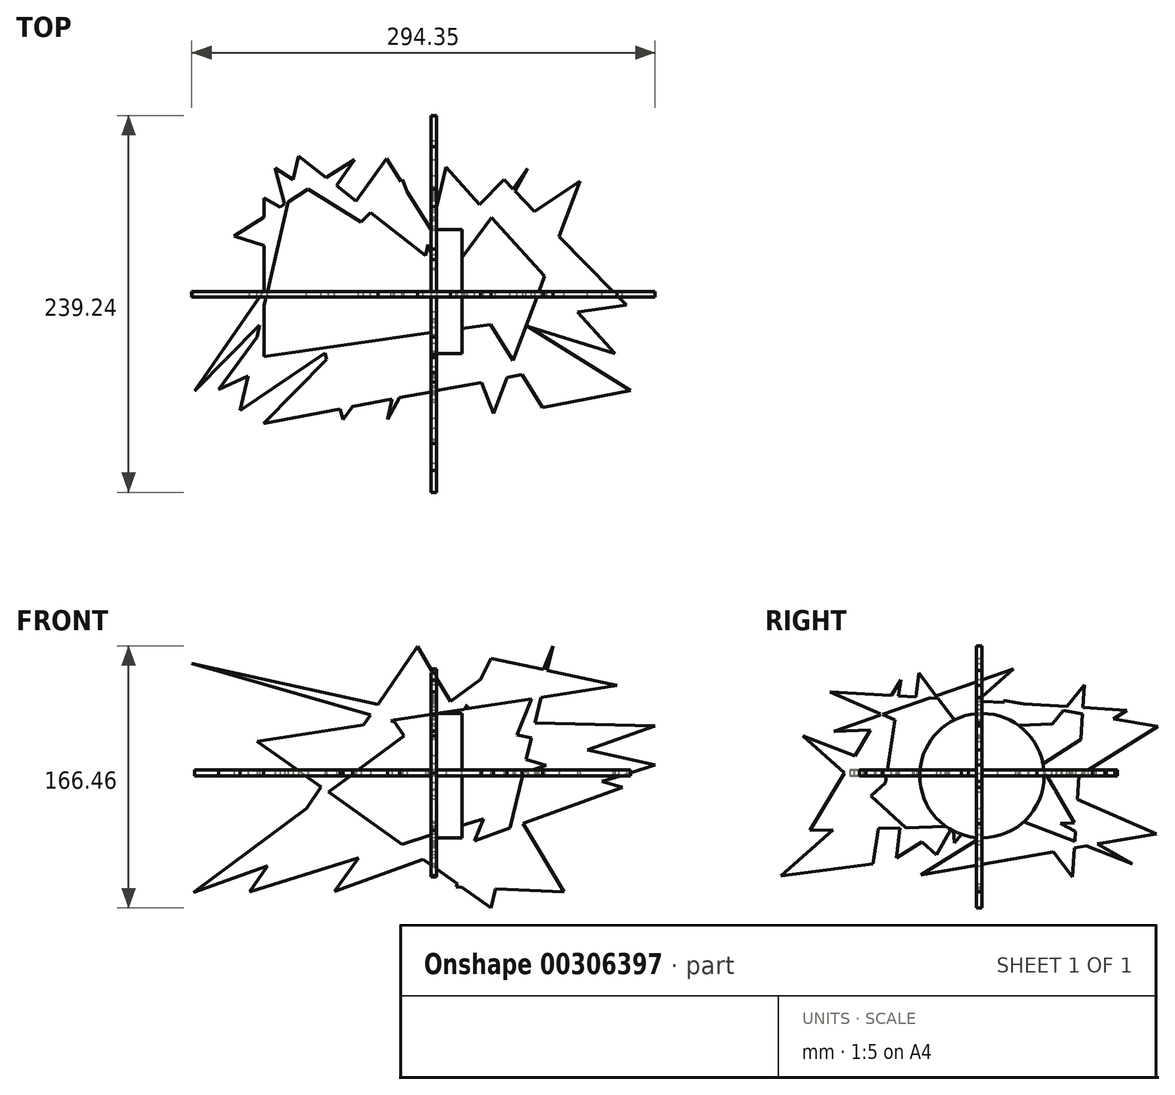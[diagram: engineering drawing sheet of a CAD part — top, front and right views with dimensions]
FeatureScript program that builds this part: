
annotation { "Feature Type Name" : "Feature", "Feature Type Description" : "" }
export const myFeature = defineFeature(function(context is Context, id is Id, definition is map)
    precondition{}
    {
        {
            var Q0;
            Q0=qCreatedBy(makeId("Front.planeOp"),FACE);
            var sketch = newSketch(context, id + "F0", { "sketchPlane" : qUnion([Q0])});
            skLineSegment(sketch, "E0", {"start": v(0, 0) * mm, "end": v(-23.78, 35.3) * mm});
            skLineSegment(sketch, "E1", {"start": v(-23.78, 35.3) * mm, "end": v(142.31, 31.7) * mm});
            skLineSegment(sketch, "E2", {"start": v(142.31, 31.7) * mm, "end": v(-150.96, -74.22) * mm});
            skLineSegment(sketch, "E3", {"start": v(-150.96, -74.22) * mm, "end": v(38.2, 66.3) * mm});
            skLineSegment(sketch, "E4", {"start": v(38.2, 66.3) * mm, "end": v(-61.25, -73.5) * mm});
            skLineSegment(sketch, "E5", {"start": v(-61.25, -73.5) * mm, "end": v(121.67, -7.43) * mm});
            skLineSegment(sketch, "E6", {"start": v(121.67, -7.43) * mm, "end": v(-152.04, 71.34) * mm});
            skLineSegment(sketch, "E7", {"start": v(-152.04, 71.34) * mm, "end": v(142.31, 6.85) * mm});
            skLineSegment(sketch, "E8", {"start": v(142.31, 6.85) * mm, "end": v(-115.3, -73.86) * mm});
            skLineSegment(sketch, "E9", {"start": v(-115.3, -73.86) * mm, "end": v(-8.65, 82.15) * mm});
            skLineSegment(sketch, "E10", {"start": v(-8.65, 82.15) * mm, "end": v(84.3, -73.86) * mm});
            skLineSegment(sketch, "E11", {"start": v(84.3, -73.86) * mm, "end": v(15.85, -70.62) * mm});
            skLineSegment(sketch, "E12", {"start": v(15.85, -70.62) * mm, "end": v(77.46, 82.5) * mm});
            skLineSegment(sketch, "E13", {"start": v(77.46, 82.5) * mm, "end": v(38.2, -83.95) * mm});
            skLineSegment(sketch, "E14", {"start": v(38.2, -83.95) * mm, "end": v(-110.37, 21.73) * mm});
            skLineSegment(sketch, "E15", {"start": v(-110.37, 21.73) * mm, "end": v(118.17, 57.29) * mm});
            skLineSegment(sketch, "E16", {"start": v(118.17, 57.29) * mm, "end": v(38.2, 74.58) * mm});
            skLineSegment(sketch, "E17", {"start": v(38.2, 74.58) * mm, "end": v(0, 0) * mm});
            skSolve(sketch);
        }
        {
            var Q0;
            Q0=qCreatedBy(makeId("Right.planeOp"),FACE);
            var sketch = newSketch(context, id + "F1", { "sketchPlane" : qUnion([Q0])});
            skLineSegment(sketch, "E18", {"start": v(0, 0) * mm, "end": v(51.5, 33.02) * mm});
            skLineSegment(sketch, "E19", {"start": v(51.5, 33.02) * mm, "end": v(-93.92, 28.17) * mm});
            skLineSegment(sketch, "E20", {"start": v(-93.92, 28.17) * mm, "end": v(20.13, 67.8) * mm});
            skLineSegment(sketch, "E21", {"start": v(20.13, 67.8) * mm, "end": v(-127.57, -63.64) * mm});
            skLineSegment(sketch, "E22", {"start": v(-127.57, -63.64) * mm, "end": v(-69.11, -55.94) * mm});
            skLineSegment(sketch, "E23", {"start": v(-69.11, -55.94) * mm, "end": v(-51.44, 60.68) * mm});
            skLineSegment(sketch, "E24", {"start": v(-51.44, 60.68) * mm, "end": v(-109.32, -34.84) * mm});
            skLineSegment(sketch, "E25", {"start": v(-109.32, -34.84) * mm, "end": v(58.63, -30) * mm});
            skLineSegment(sketch, "E26", {"start": v(58.63, -30) * mm, "end": v(13.58, 47.85) * mm});
            skLineSegment(sketch, "E27", {"start": v(13.58, 47.85) * mm, "end": v(111.67, 31.3) * mm});
            skLineSegment(sketch, "E28", {"start": v(111.67, 31.3) * mm, "end": v(-38.6, -63.07) * mm});
            skLineSegment(sketch, "E29", {"start": v(-38.6, -63.07) * mm, "end": v(110.81, -36.84) * mm});
            skLineSegment(sketch, "E30", {"start": v(110.81, -36.84) * mm, "end": v(-96.49, 53.27) * mm});
            skLineSegment(sketch, "E31", {"start": v(-96.49, 53.27) * mm, "end": v(92, 41.57) * mm});
            skLineSegment(sketch, "E32", {"start": v(92, 41.57) * mm, "end": v(-54.41, -52.3) * mm});
            skLineSegment(sketch, "E33", {"start": v(-54.41, -52.3) * mm, "end": v(-40.03, 65.24) * mm});
            skLineSegment(sketch, "E34", {"start": v(-40.03, 65.24) * mm, "end": v(57.49, -64.21) * mm});
            skLineSegment(sketch, "E35", {"start": v(57.49, -64.21) * mm, "end": v(65.04, 57.57) * mm});
            skLineSegment(sketch, "E36", {"start": v(65.04, 57.57) * mm, "end": v(-17.5, -42.54) * mm});
            skLineSegment(sketch, "E37", {"start": v(-17.5, -42.54) * mm, "end": v(-22.07, 10.5) * mm});
            skLineSegment(sketch, "E38", {"start": v(-22.07, 10.5) * mm, "end": v(95.41, -55.94) * mm});
            skLineSegment(sketch, "E39", {"start": v(95.41, -55.94) * mm, "end": v(-113.6, 25.32) * mm});
            skLineSegment(sketch, "E40", {"start": v(-113.6, 25.32) * mm, "end": v(-28.9, -50.24) * mm});
            skLineSegment(sketch, "E41", {"start": v(-28.9, -50.24) * mm, "end": v(0, 0) * mm});
            skSolve(sketch);
        }
        {
            var Q0;
            Q0=qCreatedBy(makeId("Top.planeOp"),FACE);
            var sketch = newSketch(context, id + "F2", { "sketchPlane" : qUnion([Q0])});
            skLineSegment(sketch, "E42", {"start": v(0, 0) * mm, "end": v(-106, 59.23) * mm});
            skLineSegment(sketch, "E43", {"start": v(-106, 59.23) * mm, "end": v(-106, -41.18) * mm});
            skLineSegment(sketch, "E44", {"start": v(-106, -41.18) * mm, "end": v(124.02, -8.68) * mm});
            skLineSegment(sketch, "E45", {"start": v(124.02, -8.68) * mm, "end": v(46.25, 70.91) * mm});
            skLineSegment(sketch, "E46", {"start": v(46.25, 70.91) * mm, "end": v(-106.36, -83.9) * mm});
            skLineSegment(sketch, "E47", {"start": v(-106.36, -83.9) * mm, "end": v(86.41, -47.38) * mm});
            skLineSegment(sketch, "E48", {"start": v(86.41, -47.38) * mm, "end": v(-84.1, 85.88) * mm});
            skLineSegment(sketch, "E49", {"start": v(-84.1, 85.88) * mm, "end": v(-121.33, -75.5) * mm});
            skLineSegment(sketch, "E50", {"start": v(-121.33, -75.5) * mm, "end": v(94.45, 70.18) * mm});
            skLineSegment(sketch, "E51", {"start": v(94.45, 70.18) * mm, "end": v(39.68, -77.69) * mm});
            skLineSegment(sketch, "E52", {"start": v(39.68, -77.69) * mm, "end": v(-18, 70.91) * mm});
            skLineSegment(sketch, "E53", {"start": v(-18, 70.91) * mm, "end": v(-150.13, -63.1) * mm});
            skLineSegment(sketch, "E54", {"start": v(-150.13, -63.1) * mm, "end": v(-48.68, 83.7) * mm});
            skLineSegment(sketch, "E55", {"start": v(-48.68, 83.7) * mm, "end": v(-124.99, 35.13) * mm});
            skLineSegment(sketch, "E56", {"start": v(-124.99, 35.13) * mm, "end": v(116.72, -39.35) * mm});
            skLineSegment(sketch, "E57", {"start": v(116.72, -39.35) * mm, "end": v(9.38, 78.94) * mm});
            skLineSegment(sketch, "E58", {"start": v(9.38, 78.94) * mm, "end": v(-27.58, -81.2) * mm});
            skLineSegment(sketch, "E59", {"start": v(-27.58, -81.2) * mm, "end": v(61.4, 78.04) * mm});
            skLineSegment(sketch, "E60", {"start": v(61.4, 78.04) * mm, "end": v(-55.98, -81.34) * mm});
            skLineSegment(sketch, "E61", {"start": v(-55.98, -81.34) * mm, "end": v(-99.06, 78.21) * mm});
            skLineSegment(sketch, "E62", {"start": v(-99.06, 78.21) * mm, "end": v(126.58, -63.08) * mm});
            skLineSegment(sketch, "E63", {"start": v(126.58, -63.08) * mm, "end": v(70.73, -73.66) * mm});
            skLineSegment(sketch, "E64", {"start": v(70.73, -73.66) * mm, "end": v(-28.23, 84.42) * mm});
            skLineSegment(sketch, "E65", {"start": v(-28.23, 84.42) * mm, "end": v(-134.84, -62.35) * mm});
            skLineSegment(sketch, "E66", {"start": v(-134.84, -62.35) * mm, "end": v(0, 0) * mm});
            skSolve(sketch);
        }
        {
            var Q0;
            Q0 = qSketchRegion(id + "F0", true);
            extrude(context, id + "F3", {"entities" : qUnion([Q0]), "depth" : 3.56 * mm});
        }
        {
            var Q0;
            Q0 = qSketchRegion(id + "F1", true);
            extrude(context, id + "F4", {"entities" : qUnion([Q0]), "operationType" : NewBodyOperationType.ADD, "depth" : 3.56 * mm});
        }
        {
            var Q0;
            Q0 = qSketchRegion(id + "F2", true);
            extrude(context, id + "F5", {"entities" : qUnion([Q0]), "operationType" : NewBodyOperationType.ADD, "depth" : 3.56 * mm});
        }
        {
            var Q0;
            Q0=qCreatedBy(makeId("Right.planeOp"),FACE);
            var sketch = newSketch(context, id + "F6", { "sketchPlane" : qUnion([Q0])});
            skCircle(sketch, "E67", {"center": v(0, 0) * mm, "radius": 39.52 * mm});
            skSolve(sketch);
        }
        {
            var Q0;
            Q0 = qSketchRegion(id + "F6", true);
            extrude(context, id + "F7", {"entities" : qUnion([Q0]), "operationType" : NewBodyOperationType.ADD, "depth" : 19.8 * mm});
        }
    });
